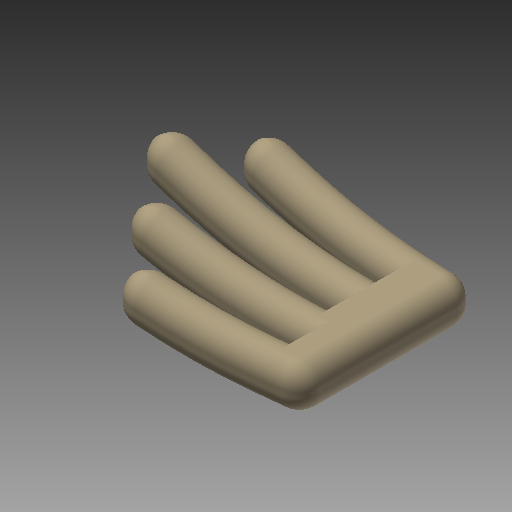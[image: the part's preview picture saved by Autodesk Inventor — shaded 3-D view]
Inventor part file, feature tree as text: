
AUTODESK INVENTOR PART (.ipt)
format: ipt  version: 2022 (Build 260153000, 153)  size: 637,440 bytes
history: native  units: mm (DEFAULTED — no unit token found)
features: other x3, plane x1
ambient origin geometry x8: Origin, YZ Plane, XZ Plane, XY Plane, X Axis, Y Axis, Z Axis, Center Point
bodies: Solid1 (feature_tree)
feature tree (4):
  other  "iMandy - FINGERS LEFT"
  plane  "Work Plane1"
  other  "Work Axis1"
  other  "Solid1::iMike - FINGERS LEFT.ipt"
